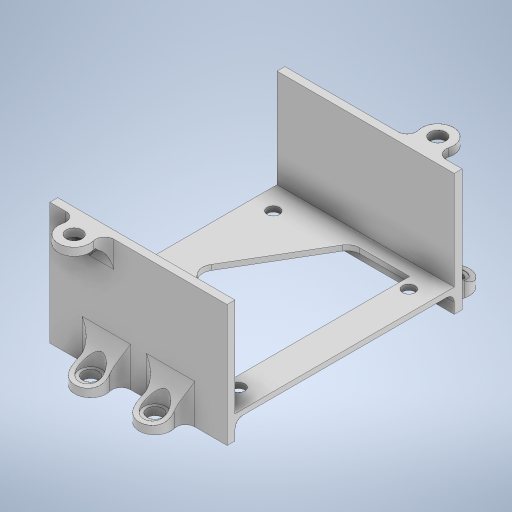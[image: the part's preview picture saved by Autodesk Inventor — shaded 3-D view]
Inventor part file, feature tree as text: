
AUTODESK INVENTOR PART (.ipt)
format: ipt  version: 2024 (Build 280153000, 153)  size: 641,536 bytes
history: native  units: in
note: dims shown in document units (in); Inventor stores cm internally (conversion verified against a paired STEP export)
features: extrude x9, fillet x3, sketch x3, plane x1, projected_geometry x1
ambient origin geometry x8: Origin, YZ Plane, XZ Plane, XY Plane, X Axis, Y Axis, Z Axis, Center Point
bodies: Solid1 (feature_tree)
feature tree (17):
  extrude  "Extrusion1"  Depth=0.1181in
  extrude  "Extrusion2"  Depth=0.1969in
  extrude  "Extrusion6"  Depth=0.4724in
  extrude  "Extrusion7"  Depth=0.4724in
  extrude  "Extrusion8"  Depth=2.6575in
  plane  "Work Plane1"
  extrude  "Extrusion9"  Depth=1.3287in
  fillet  "Fillet2"  Radius=1.6437in
  fillet  "Fillet7"  Radius=0.0787in
  extrude  "Extrusion10"  Depth=1.5551in TaperAngle=0.0deg
  extrude  "Extrusion11"  Depth=0.185in
  extrude  "Extrusion12"  Depth=0.313in
  fillet  "Fillet8"  Radius=0.313in
  sketch  "Sketch9"  dims[d0=3.2874in d1=0.1181in]
  sketch  "Sketch10"  dims[d2=0.1181in d4=0.1969in]
  sketch  "Sketch11"  dims[d5=0.1969in d6=0.4724in d7=0.4724in d8=2.6575in d9=1.3287in d10=1.6437in d11=0.0787in d12=0.0in d13=1.5551in d14=0.2756in d15=0.0in d16=0.0in d35=0.185in d36=0.313in d38=0.313in d40=0.1181in d41=0.0in d46=0.2362in d47=0.2362in d48=0.2362in d49=0.2362in d51=0.4724in d54=0.1378in d55=0.9646in d56=1.9291in d57=0.4823in d58=0.9646in d59=0.5906in d60=0.0in d61=0.3346in d62=0.3346in d63=0.3346in d64=0.3346in d65=0.4724in d66=0.0in d67=1.1811in d68=0.1181in d69=0.1969in d70=0.0in d72=0.3346in d73=2.5512in d74=1.2756in d75=2.7559in d76=0.0in d77=0.1969in d80=0.1181in d85=0.1181in d87=0.0662in d90=0.2362in d91=0.4724in d92=0.2756in d93=1.4567in d94=2.6575in d95=0.6004in d96=0.3937in d97=0.0in d100=0.4724in d102=0.2756in d103=0.0in d105=0.1181in d106=0.315in d107=0.315in d108=0.1181in d111=0.0in d112=0.0in d113=0.0591in d31=0.0197in d32=0.0344in d33=0.0197in d34=0.0344in]
  projected_geometry  "Projected Loop3"
